# Revit family: 640235
name_source: partatom
category: Specialty Equipment
units: mm (PartAtom-declared; Revit-internal decimal feet)

## family parameters
Always vertical = Yes
Cut with Voids When Loaded = No
OmniClass Number = 23.40.40.14
OmniClass Title = Food Service Equipment
Part Type = Normal
Room Calculation Point = No
Round Connector Dimension = Use Diameter
Shared = No
Work Plane-Based = No

## types (1)
- 640235
    Altezza = 451 mm  [stored 1.47966 ft]
    Assembly Code = E1090320
    Corrente di funzionamento normale = 2 A
    Default Elevation = 0 mm  [stored 0 ft]
    Description = AQUA + EB REVERSE OSMOSIS WATER TREATMENT OF 240L/H HARDNESS UP TO 35°
    Fase = 1
    Frequenza = 50 Hz
    KCLRef = KCL2C9,,e33c45b9-8928-4499-a97e-a97433608124,AC,AQUA+EB,637943765559021678,0d1accc8-c5fe-4c16-a329-9e799c2ee48f,882cc231-1f55-4f07-b128-6c81de75401e
    Lunghezza = 275 mm
    Manufacturer = COMENDA
    Model = 640235
    Numero dei poli = 1
    Peso netto = 25.00 kg
    Pessione minima acqua fredda = 150000.0 Pa
    Potenza elettrica = 250 W
    Pressione massima acqua fredda = 600000.0 Pa
    Profondità = 425 mm  [stored 1.39436 ft]
    Temperatura raccomandata per acqua fredda = 43 °C
    Tensione = 230 V
    URL = www.comenda.eu
    URL catalogo = https://www.comenda.eu

note: [stored X ft] marks values corroborated as IEEE doubles in the binary element streams (Revit-internal decimal feet)

## geometry (parser evidence)
native form markers: Sweep x2
no freeform markers — native parametric forms only
